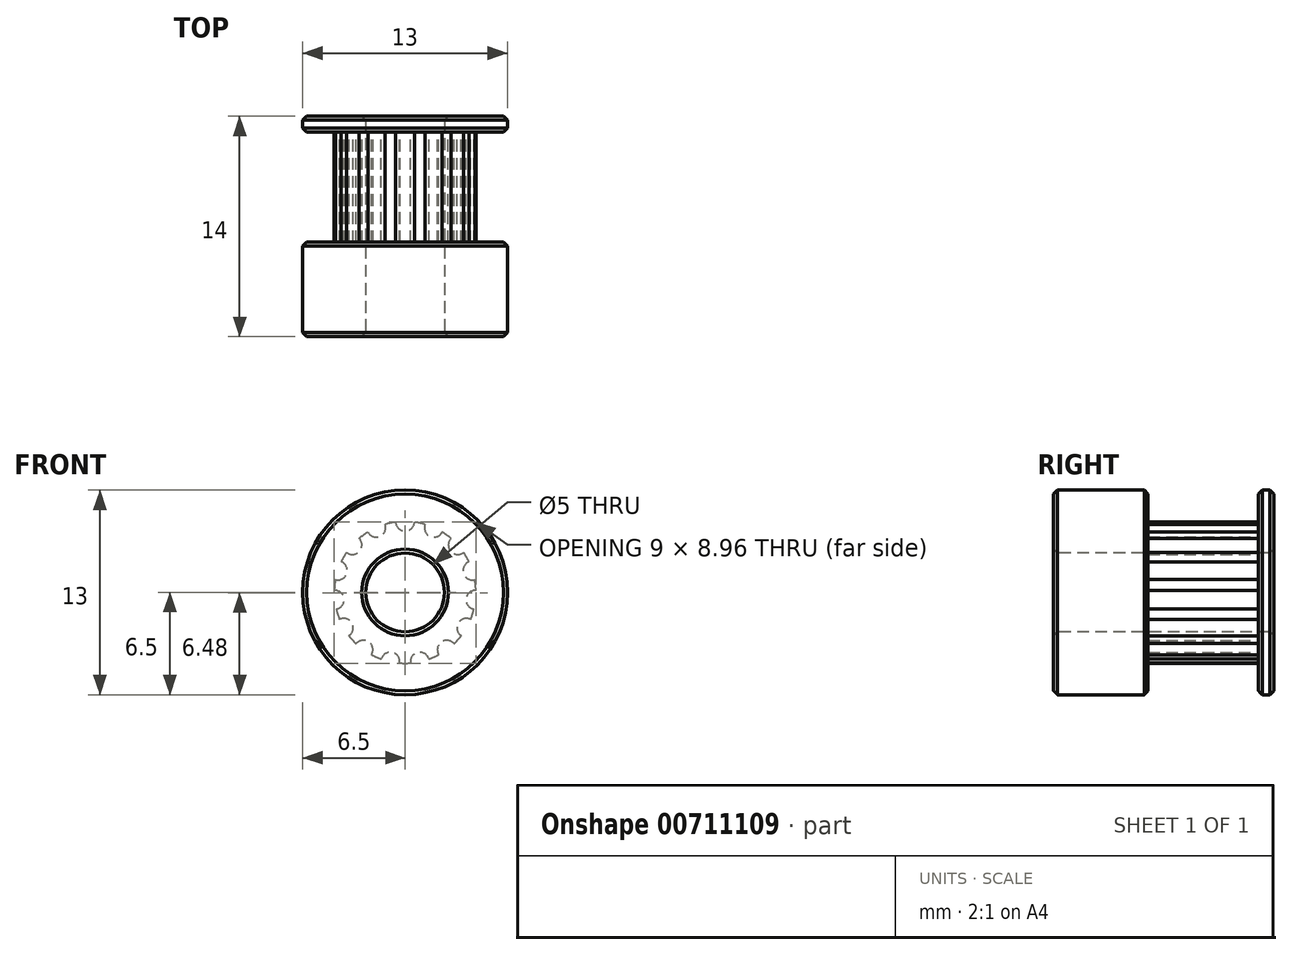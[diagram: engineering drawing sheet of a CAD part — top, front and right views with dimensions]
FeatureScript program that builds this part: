
annotation { "Feature Type Name" : "Feature", "Feature Type Description" : "" }
export const myFeature = defineFeature(function(context is Context, id is Id, definition is map)
    precondition{}
    {
        {
            var Q0;
            Q0=qCreatedBy(makeId("Front.planeOp"),FACE);
            var sketch = newSketch(context, id + "F0", { "sketchPlane" : qUnion([Q0])});
            skCircle(sketch, "E0", {"center": v(0, 0) * mm, "radius": 6.5 * mm});
            skSolve(sketch);
        }
        {
            var Q0;
            Q0=makeQuery(id+"F0.imprint","IMPRINT",FACE,{"disambiguationData":[TD([[makeQuery(id+"F0.imprint","IMPRINT",EDGE,{"derivedFrom":sQuery(id+"F0.wireOp",EDGE,"E0")}),1.0]])]});
            extrude(context, id + "F1", {"entities" : qUnion([Q0]), "depth" : 1 * mm, "offsetDistance" : 25 * mm});
        }
        {
            var Q0;
            Q0=makeQuery(id+"F1.opExtrude","CAP_FACE",FACE,{"disambiguationData":[OSD([sQuery(id+"F0.wireOp",EDGE,"E0")])],"isStart":false});
            var sketch = newSketch(context, id + "F2", { "sketchPlane" : qUnion([Q0])});
            skCircle(sketch, "E1", {"center": v(0, 0) * mm, "radius": 4.5 * mm});
            skSolve(sketch);
        }
        {
            var Q0;
            Q0=qSketchRegion(id+"F2",true);
            extrude(context, id + "F3", {"entities" : qUnion([Q0]), "operationType" : NewBodyOperationType.ADD, "depth" : 7 * mm, "offsetDistance" : 25 * mm});
        }
        {
            var Q0;
            Q0=makeQuery(id+"F3.opExtrude","CAP_FACE",FACE,{"disambiguationData":[OSD([sQuery(id+"F2.wireOp",EDGE,"E1")])],"isStart":false});
            var sketch = newSketch(context, id + "F4", { "sketchPlane" : qUnion([Q0])});
            skCircle(sketch, "E2", {"center": v(0, 0) * mm, "radius": 6.5 * mm});
            skSolve(sketch);
        }
        {
            var Q0;
            Q0=qSketchRegion(id+"F4",true);
            extrude(context, id + "F5", {"entities" : qUnion([Q0]), "operationType" : NewBodyOperationType.ADD, "depth" : 6 * mm, "offsetDistance" : 25 * mm});
        }
        {
            var Q0;
            Q0=makeQuery(id+"F1.opExtrude","CAP_FACE",FACE,{"disambiguationData":[OSD([sQuery(id+"F0.wireOp",EDGE,"E0")])],"isStart":false});
            var sketch = newSketch(context, id + "F6", { "sketchPlane" : qUnion([Q0])});
            skCircle(sketch, "E3", {"center": v(0, 0) * mm, "radius": 5 * mm, "construction": true});
            skLineSegment(sketch, "E4", {"start": v(-4.5, 0) * mm, "end": v(0, 0) * mm, "construction": true});
            skLineSegment(sketch, "E5", {"start": v(0, 0) * mm, "end": v(0, 4.5) * mm, "construction": true});
            skCircle(sketch, "E6", {"center": v(0, 4.5) * mm, "radius": 0.6 * mm});
            skCircle(sketch, "E7.1.0", {"center": v(-1.83, 4.11) * mm, "radius": 0.6 * mm});
            skCircle(sketch, "E7.2.0", {"center": v(-3.34, 3.01) * mm, "radius": 0.6 * mm});
            skCircle(sketch, "E7.3.0", {"center": v(-4.28, 1.4) * mm, "radius": 0.6 * mm});
            skCircle(sketch, "E7.4.0", {"center": v(-4.48, -0.47) * mm, "radius": 0.6 * mm});
            skCircle(sketch, "E7.5.0", {"center": v(-3.9, -2.25) * mm, "radius": 0.6 * mm});
            skCircle(sketch, "E7.6.0", {"center": v(-2.65, -3.64) * mm, "radius": 0.6 * mm});
            skCircle(sketch, "E7.7.0", {"center": v(-0.94, -4.4) * mm, "radius": 0.6 * mm});
            skCircle(sketch, "E7.8.0", {"center": v(0.94, -4.4) * mm, "radius": 0.6 * mm});
            skCircle(sketch, "E7.9.0", {"center": v(2.65, -3.64) * mm, "radius": 0.6 * mm});
            skCircle(sketch, "E7.10.0", {"center": v(3.9, -2.25) * mm, "radius": 0.6 * mm});
            skCircle(sketch, "E7.11.0", {"center": v(4.48, -0.47) * mm, "radius": 0.6 * mm});
            skCircle(sketch, "E7.12.0", {"center": v(4.28, 1.4) * mm, "radius": 0.6 * mm});
            skCircle(sketch, "E7.13.0", {"center": v(3.34, 3.01) * mm, "radius": 0.6 * mm});
            skCircle(sketch, "E7.14.0", {"center": v(1.83, 4.11) * mm, "radius": 0.6 * mm});
            skSolve(sketch);
        }
        {
            var Q0;
            Q0=qSketchRegion(id+"F6",true);
            var Q1;
            Q1=makeQuery(id+"F5.opExtrude","CAP_FACE",FACE,{"disambiguationData":[OSD([sQuery(id+"F4.wireOp",EDGE,"E2")])],"isStart":true});
            extrude(context, id + "F7", {"entities" : qUnion([Q0]), "operationType" : NewBodyOperationType.REMOVE, "endBound" : BoundingType.UP_TO_SURFACE, "depth" : 7.5 * mm, "endBoundEntityFace" : qUnion([Q1]), "offsetDistance" : 25 * mm});
        }
        {
            var Q0;
            Q0=makeQuery(id+"F5.opExtrude","CAP_FACE",FACE,{"disambiguationData":[OSD([sQuery(id+"F4.wireOp",EDGE,"E2")])],"isStart":false});
            var sketch = newSketch(context, id + "F8", { "sketchPlane" : qUnion([Q0])});
            skCircle(sketch, "E8", {"center": v(0, 0) * mm, "radius": 2.5 * mm});
            skSolve(sketch);
        }
        {
            var Q0;
            Q0=qSketchRegion(id+"F8",true);
            extrude(context, id + "F9", {"entities" : qUnion([Q0]), "operationType" : NewBodyOperationType.REMOVE, "endBound" : BoundingType.THROUGH_ALL, "oppositeDirection" : true, "depth" : 25 * mm, "offsetDistance" : 25 * mm});
        }
        {
            var Q0;
            Q0=makeQuery(id+"F5.opExtrude","SWEPT_FACE",FACE,{"disambiguationData":[OSD([sQuery(id+"F4.wireOp",EDGE,"E2")])]});
            var Q1;
            Q1=makeQuery(id+"F1.opExtrude","SWEPT_FACE",FACE,{"disambiguationData":[OSD([sQuery(id+"F0.wireOp",EDGE,"E0")])]});
            var Q2;
            Q2=makeQuery(id+"F9.boolean.opBoolean","COPY",FACE,{"derivedFrom":makeQuery(id+"F9.opExtrude","SWEPT_FACE",FACE,{"disambiguationData":[OSD([sQuery(id+"F8.wireOp",EDGE,"E8")])]})});
            chamfer(context, id + "F10", {"entities" : qUnion([Q0, Q1, Q2]), "width" : 0.25 * mm, "tangentPropagation" : true});
        }
    });
